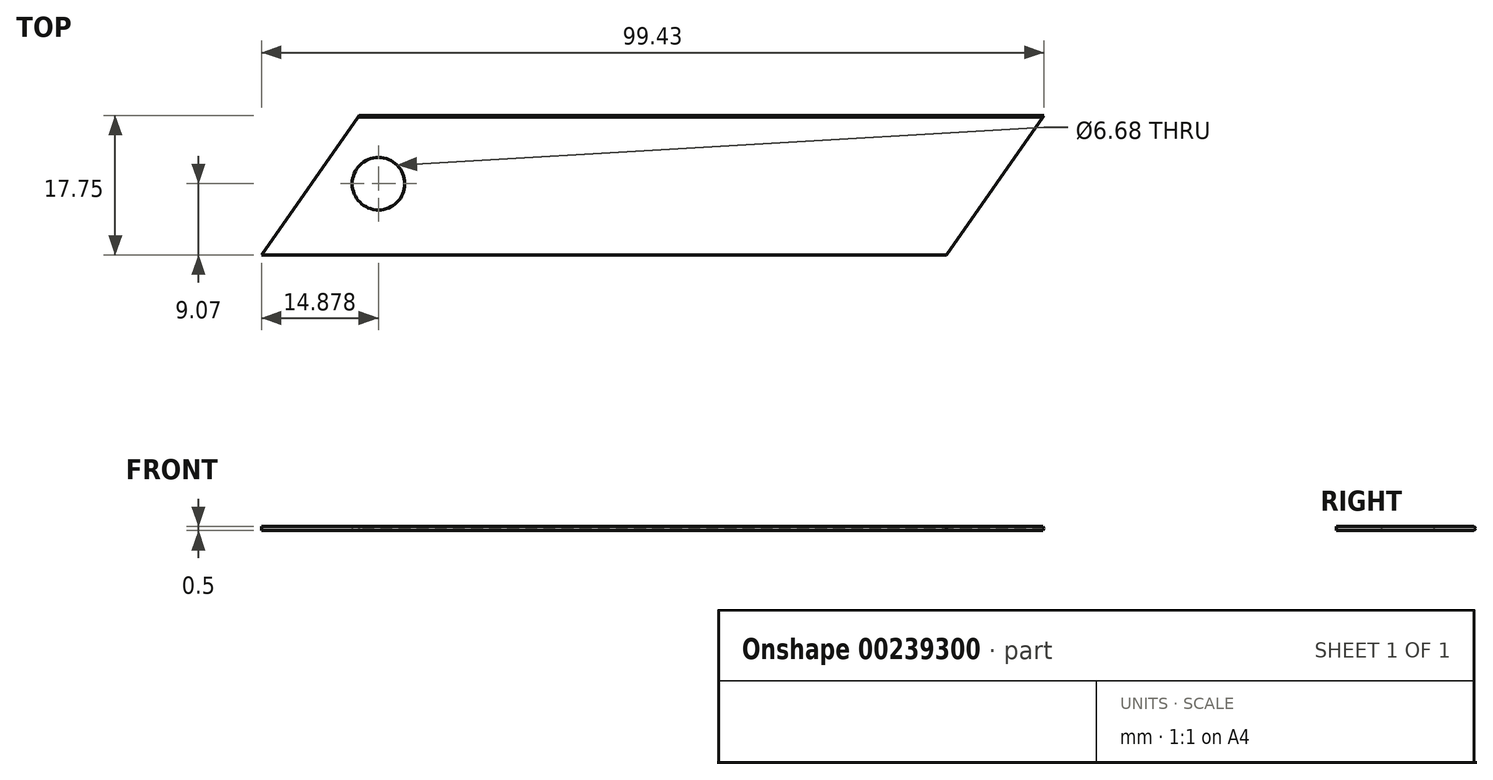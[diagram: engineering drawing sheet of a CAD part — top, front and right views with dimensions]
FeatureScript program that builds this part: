
annotation { "Feature Type Name" : "Feature", "Feature Type Description" : "" }
export const myFeature = defineFeature(function(context is Context, id is Id, definition is map)
    precondition{}
    {
        {
            var Q0;
            Q0=qCreatedBy(makeId("Top.planeOp"),FACE);
            var sketch = newSketch(context, id + "F0", { "sketchPlane" : qUnion([Q0])});
            skLineSegment(sketch, "E0.bottom", {"start": v(3.62, -9.07) * mm, "end": v(90.62, -9.07) * mm});
            skLineSegment(sketch, "E0.top", {"start": v(16.23, 8.93) * mm, "end": v(103.23, 8.93) * mm});
            skLineSegment(sketch, "E1", {"start": v(16.23, 8.93) * mm, "end": v(3.62, -9.07) * mm});
            skLineSegment(sketch, "E2", {"start": v(103.23, 8.93) * mm, "end": v(90.62, -9.07) * mm});
            skPoint(sketch, "E3.orphan", {"position": v(90.62, -9.07) * mm});
            skCircle(sketch, "E4", {"center": v(18.5, 0) * mm, "radius": 3.34 * mm});
            skPoint(sketch, "E5.orphan", {"position": v(95.93, -9.07) * mm});
            skSolve(sketch);
        }
        {
            var Q0;
            Q0 = qSketchRegion(id + "F0", true);
            extrude(context, id + "F1", {"entities" : qUnion([Q0]), "depth" : .5 * mm});
        }
        {
            var Q0;
            Q0=makeQuery(id+"F1.opExtrude","CAP_EDGE",EDGE,{"disambiguationData":[OSD([sQuery(id+"F0.wireOp",EDGE,"E0.top")])],"isStart":false});
            var Q1;
            Q1=makeQuery(id+"F1.opExtrude","CAP_EDGE",EDGE,{"disambiguationData":[OSD([sQuery(id+"F0.wireOp",EDGE,"E0.top")])],"isStart":true});
            chamfer(context, id + "F2", {"entities" : qUnion([Q0, Q1]), "width" : .5 * mm, "tangentPropagation" : true});
        }
    });
